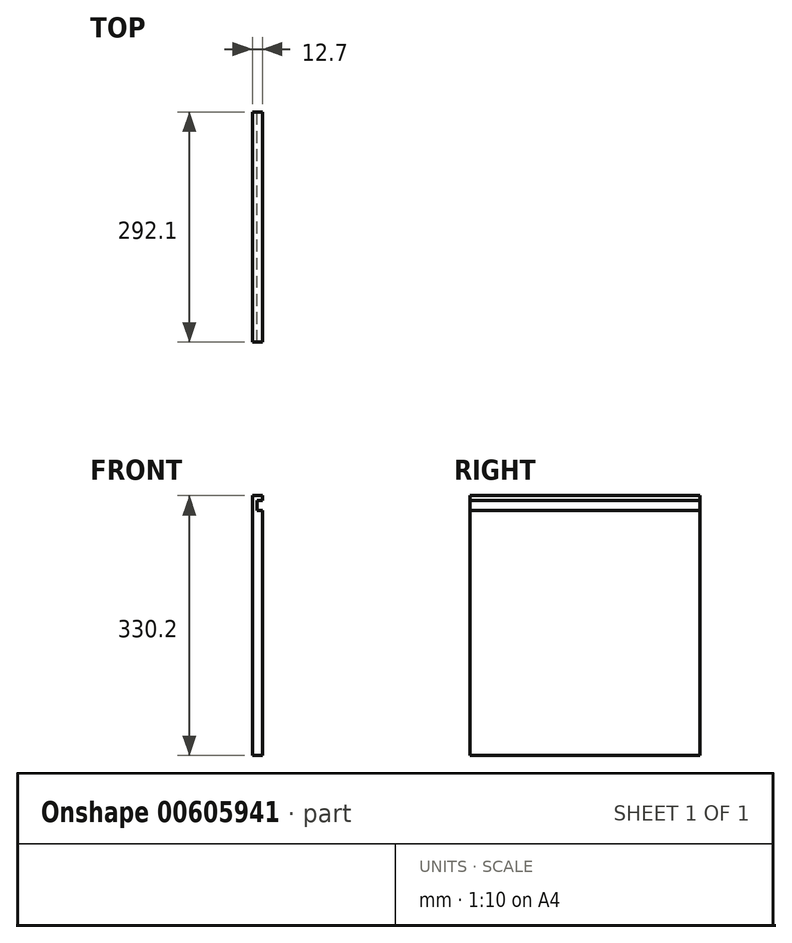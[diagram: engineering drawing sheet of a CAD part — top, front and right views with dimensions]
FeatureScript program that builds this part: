
annotation { "Feature Type Name" : "Feature", "Feature Type Description" : "" }
export const myFeature = defineFeature(function(context is Context, id is Id, definition is map)
    precondition{}
    {
        {
            var Q0;
            Q0=qCreatedBy(makeId("Right.planeOp"),FACE);
            var sketch = newSketch(context, id + "F0", { "sketchPlane" : qUnion([Q0])});
            skLineSegment(sketch, "E0.bottom", {"start": v(0, 0) * mm, "end": v(-292.1, 0) * mm});
            skLineSegment(sketch, "E0.top", {"start": v(0, 304.8) * mm, "end": v(-292.1, 304.8) * mm});
            skLineSegment(sketch, "E0.left", {"start": v(0, 0) * mm, "end": v(0, 304.8) * mm});
            skLineSegment(sketch, "E0.right", {"start": v(-292.1, 0) * mm, "end": v(-292.1, 304.8) * mm});
            skSolve(sketch);
        }
        {
            var Q0;
            Q0=makeQuery(id+"F0.imprint","IMPRINT",FACE,{"disambiguationData":[TD([[makeQuery(id+"F0.imprint","IMPRINT",EDGE,{"derivedFrom":sQuery(id+"F0.wireOp",EDGE,"E0.bottom")}),-1.0]])]});
            extrude(context, id + "F1", {"entities" : qUnion([Q0]), "depth" : 12.7 * mm, "offsetDistance" : 25.4 * mm});
        }
        {
            var Q0;
            Q0=qCreatedBy(makeId("Right.planeOp"),FACE);
            var sketch = newSketch(context, id + "F2", { "sketchPlane" : qUnion([Q0])});
            skLineSegment(sketch, "E1.bottom", {"start": v(0, 0) * mm, "end": v(-292.1, 0) * mm});
            skLineSegment(sketch, "E1.top", {"start": v(0, -25.4) * mm, "end": v(-292.1, -25.4) * mm});
            skLineSegment(sketch, "E1.left", {"start": v(0, 0) * mm, "end": v(0, -25.4) * mm});
            skLineSegment(sketch, "E1.right", {"start": v(-292.1, 0) * mm, "end": v(-292.1, -25.4) * mm});
            skSolve(sketch);
        }
        {
            var Q0;
            Q0=makeQuery(id+"F2.imprint","IMPRINT",FACE,{"disambiguationData":[TD([[makeQuery(id+"F2.imprint","IMPRINT",EDGE,{"derivedFrom":sQuery(id+"F2.wireOp",EDGE,"E1.bottom")}),1.0]])]});
            extrude(context, id + "F3", {"entities" : qUnion([Q0]), "operationType" : NewBodyOperationType.ADD, "depth" : 12.7 * mm, "offsetDistance" : 25.4 * mm});
        }
        {
            var Q0;
            Q0=makeQuery(id+"F3.boolean.opBoolean","MERGE",FACE,{"derivedFrom":[makeQuery(id+"F1.opExtrude","CAP_FACE",FACE,{"disambiguationData":[OSD([sQuery(id+"F0.wireOp",EDGE,"E0.bottom"),sQuery(id+"F0.wireOp",EDGE,"E0.top"),sQuery(id+"F0.wireOp",EDGE,"E0.left"),sQuery(id+"F0.wireOp",EDGE,"E0.right")])],"isStart":false}),makeQuery(id+"F3.opExtrude","CAP_FACE",FACE,{"disambiguationData":[OSD([sQuery(id+"F2.wireOp",EDGE,"E1.bottom"),sQuery(id+"F2.wireOp",EDGE,"E1.top"),sQuery(id+"F2.wireOp",EDGE,"E1.left"),sQuery(id+"F2.wireOp",EDGE,"E1.right")])],"isStart":false})]});
            var sketch = newSketch(context, id + "F4", { "sketchPlane" : qUnion([Q0])});
            skLineSegment(sketch, "E2", {"start": v(-292.1, 304.8) * mm, "end": v(-292.1, 298.45) * mm});
            skLineSegment(sketch, "E3", {"start": v(-292.1, 298.45) * mm, "end": v(-292.1, 285.75) * mm});
            skLineSegment(sketch, "E4", {"start": v(-292.1, 285.75) * mm, "end": v(0, 285.75) * mm});
            skLineSegment(sketch, "E5", {"start": v(0, 285.75) * mm, "end": v(0, 298.45) * mm});
            skLineSegment(sketch, "E6", {"start": v(0, 298.45) * mm, "end": v(-292.1, 298.45) * mm});
            skSolve(sketch);
        }
        {
            var Q0;
            Q0=makeQuery(id+"F4.imprint","IMPRINT",FACE,{"disambiguationData":[TD([[makeQuery(id+"F4.imprint","IMPRINT",EDGE,{"derivedFrom":sQuery(id+"F4.wireOp",EDGE,"E3")}),-1.0]])]});
            extrude(context, id + "F5", {"entities" : qUnion([Q0]), "operationType" : NewBodyOperationType.REMOVE, "oppositeDirection" : true, "depth" : 6.35 * mm, "offsetDistance" : 25.4 * mm});
        }
    });
